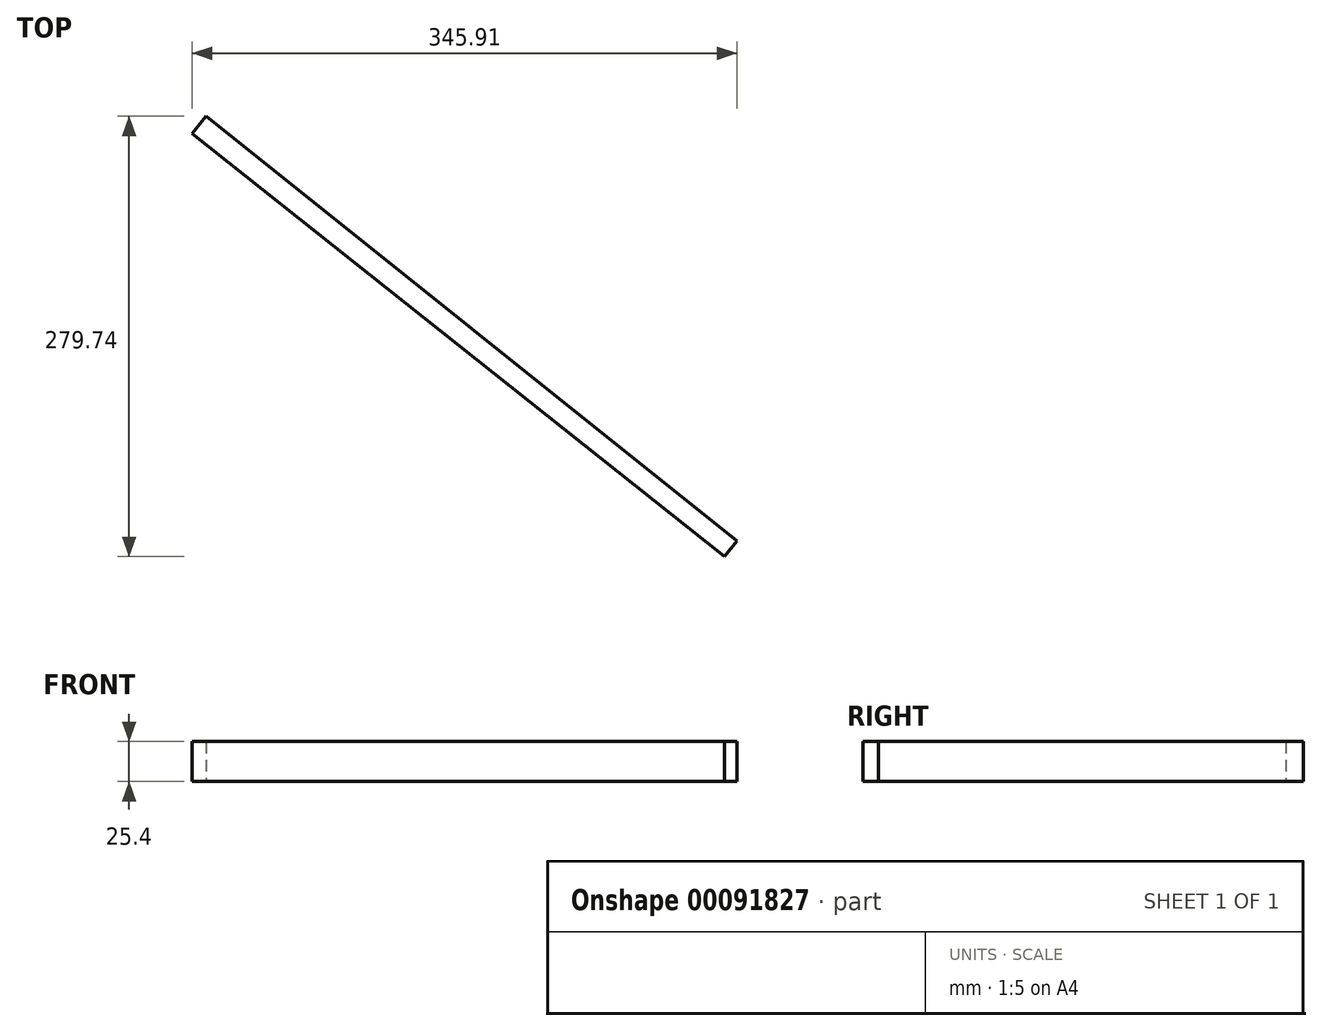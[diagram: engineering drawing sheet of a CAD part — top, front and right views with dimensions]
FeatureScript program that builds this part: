
annotation { "Feature Type Name" : "Feature", "Feature Type Description" : "" }
export const myFeature = defineFeature(function(context is Context, id is Id, definition is map)
    precondition{}
    {
        {
            var Q0;
            Q0=qCreatedBy(makeId("Top.planeOp"),FACE);
            var sketch = newSketch(context, id + "F0", { "sketchPlane" : qUnion([Q0])});
            skLineSegment(sketch, "E0", {"start": v(0, 0) * mm, "end": v(337.1, -269.84) * mm});
            skLineSegment(sketch, "E1", {"start": v(-8.8, -10.95) * mm, "end": v(329.13, -279.74) * mm});
            skLineSegment(sketch, "E2", {"start": v(329.13, -279.74) * mm, "end": v(337.1, -269.84) * mm});
            skLineSegment(sketch, "E3", {"start": v(-8.8, -10.95) * mm, "end": v(0, 0) * mm});
            skSolve(sketch);
        }
        {
            var Q0;
            Q0=makeQuery(id+"F0.imprint","IMPRINT",FACE,{"disambiguationData":[TD([[makeQuery(id+"F0.imprint","IMPRINT",EDGE,{"derivedFrom":sQuery(id+"F0.wireOp",EDGE,"E0")}),-1.0]])]});
            extrude(context, id + "F1", {"entities" : qUnion([Q0]), "depth" : 25.4 * mm});
        }
    });
